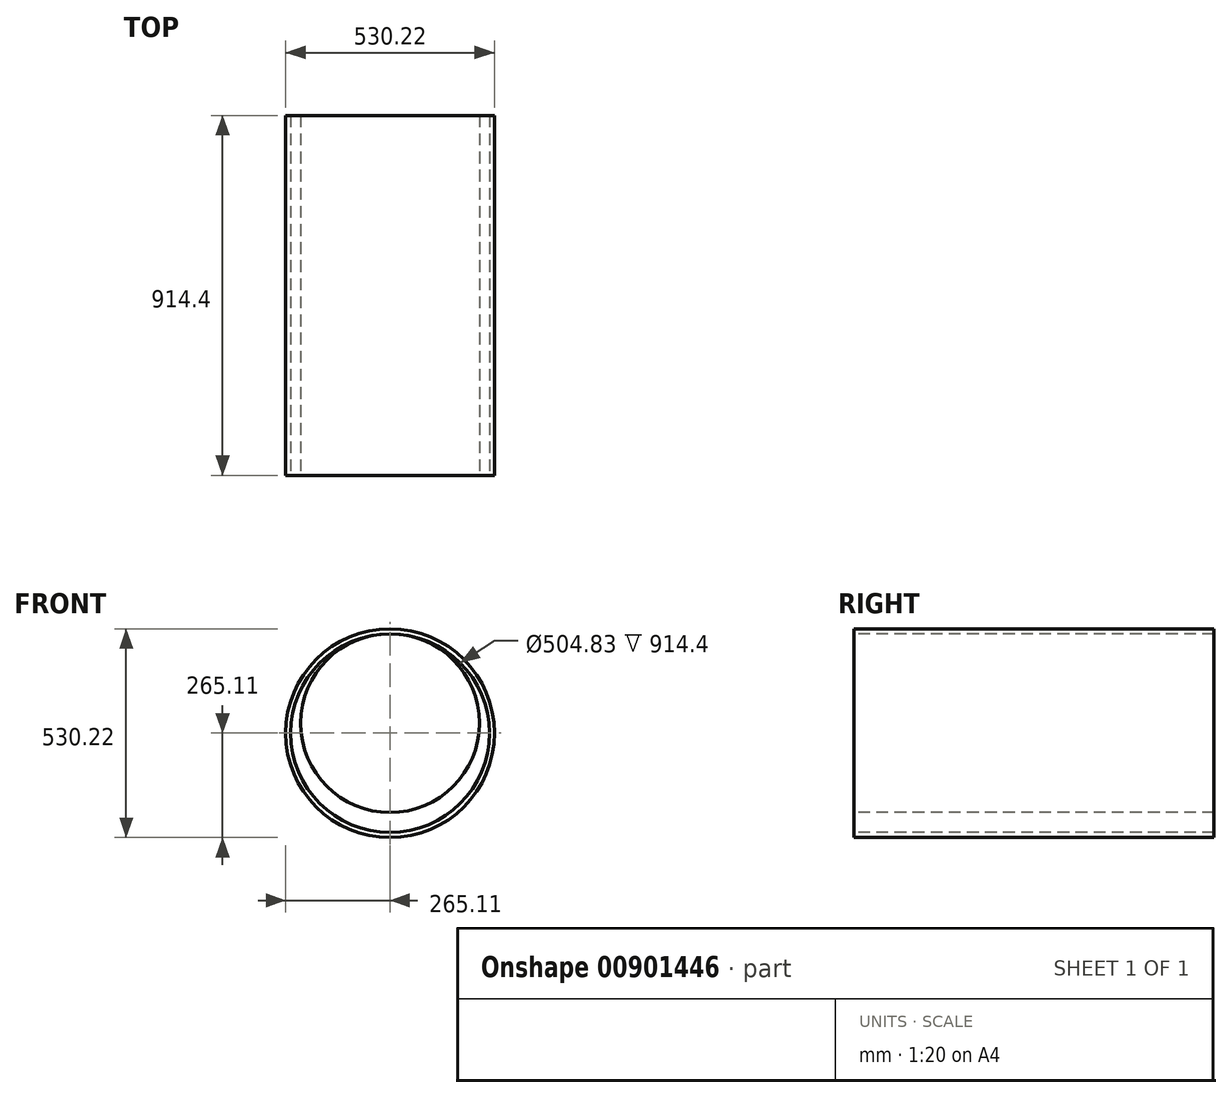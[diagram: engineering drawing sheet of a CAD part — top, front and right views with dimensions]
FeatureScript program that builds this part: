
annotation { "Feature Type Name" : "Feature", "Feature Type Description" : "" }
export const myFeature = defineFeature(function(context is Context, id is Id, definition is map)
    precondition{}
    {
        {
            var Q0;
            Q0=qCreatedBy(makeId("Front.planeOp"),FACE);
            var sketch = newSketch(context, id + "F0", { "sketchPlane" : qUnion([Q0])});
            skCircle(sketch, "E0", {"center": v(0, 0) * mm, "radius": 227.01 * mm});
            skSolve(sketch);
        }
        {
            var Q0;
            Q0 = qSketchRegion(id + "F0", true);
            extrude(context, id + "F1", {"entities" : qUnion([Q0]), "oppositeDirection" : true, "depth" : 914.4 * mm, "offsetDistance" : 25.4 * mm});
        }
        {
            var Q0;
            Q0=makeQuery(id+"F1.opExtrude","CAP_FACE",FACE,{"disambiguationData":[OSD([sQuery(id+"F0.wireOp",EDGE,"E0")])],"isStart":true});
            var sketch = newSketch(context, id + "F2", { "sketchPlane" : qUnion([Q0])});
            skCircle(sketch, "E1", {"center": v(0, -25.4) * mm, "radius": 252.41 * mm});
            skCircle(sketch, "E2", {"center": v(0, -25.4) * mm, "radius": 265.11 * mm});
            skLineSegment(sketch, "E3", {"start": v(0, 0) * mm, "end": v(0, 227.01) * mm, "construction": true});
            skLineSegment(sketch, "E4", {"start": v(0, -25.4) * mm, "end": v(0, 227.01) * mm});
            skLineSegment(sketch, "E5", {"start": v(0, 0) * mm, "end": v(-251.13, 0) * mm});
            skLineSegment(sketch, "E6", {"start": v(0, -25.4) * mm, "end": v(-252.41, -25.4) * mm});
            skSolve(sketch);
        }
        {
            var Q0;
            Q0 = qSketchRegion(id + "F2", true);
            extrude(context, id + "F3", {"entities" : qUnion([Q0]), "operationType" : NewBodyOperationType.ADD, "oppositeDirection" : true, "depth" : 914.4 * mm, "offsetDistance" : 25.4 * mm});
        }
    });
